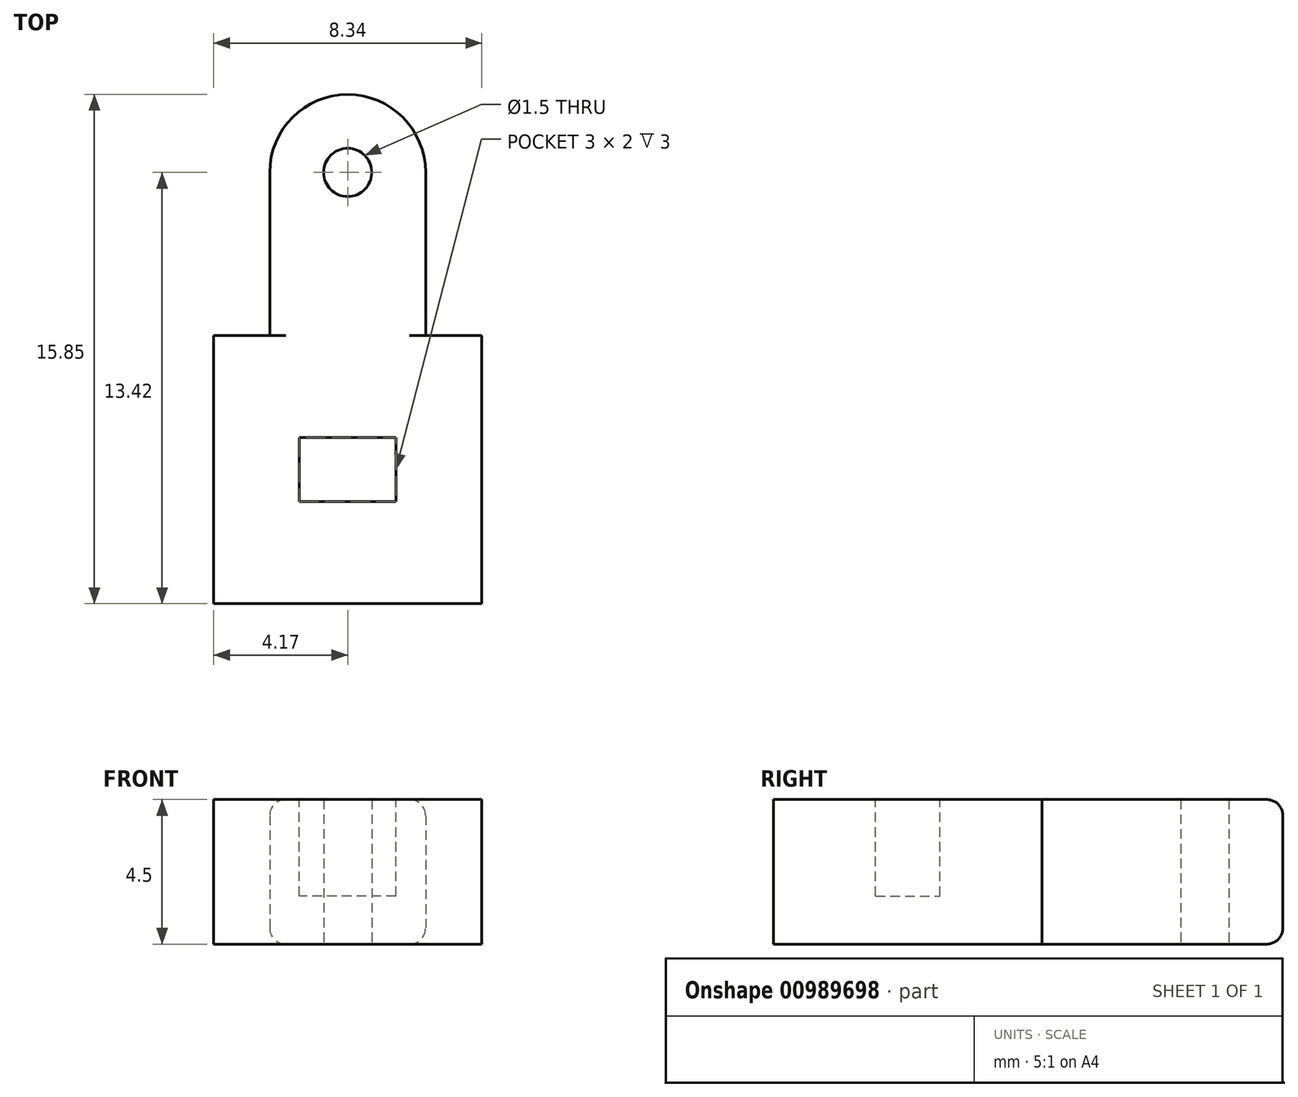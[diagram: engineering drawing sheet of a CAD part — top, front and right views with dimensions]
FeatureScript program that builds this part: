
annotation { "Feature Type Name" : "Feature", "Feature Type Description" : "" }
export const myFeature = defineFeature(function(context is Context, id is Id, definition is map)
    precondition{}
    {
        {
            var Q0;
            Q0=qCreatedBy(makeId("Top.planeOp"),FACE);
            var sketch = newSketch(context, id + "F0", { "sketchPlane" : qUnion([Q0])});
            skLineSegment(sketch, "E0.bottom", {"start": v(-4.18, 4.18) * mm, "end": v(4.18, 4.17) * mm});
            skLineSegment(sketch, "E0.top", {"start": v(-4.18, -4.17) * mm, "end": v(4.18, -4.18) * mm});
            skLineSegment(sketch, "E0.left", {"start": v(-4.17, 4.18) * mm, "end": v(-4.18, -4.18) * mm});
            skLineSegment(sketch, "E0.right", {"start": v(4.18, 4.18) * mm, "end": v(4.17, -4.18) * mm});
            skLineSegment(sketch, "E1", {"start": v(0, 4.17) * mm, "end": v(0, 11.67) * mm, "construction": true});
            skLineSegment(sketch, "E2", {"start": v(-2.42, 4.17) * mm, "end": v(-2.43, 9.25) * mm});
            skLineSegment(sketch, "E3", {"start": v(2.42, 4.17) * mm, "end": v(2.43, 9.25) * mm});
            skArc(sketch, "E4", {"start": v(2.42, 9.25) * mm, "mid": v(0, 11.67) * mm, "end": v(-2.43, 9.25) * mm});
            skCircle(sketch, "E5", {"center": v(0, 9.25) * mm, "radius": 0.75 * mm});
            skSolve(sketch);
        }
        {
            var Q0;
            Q0=makeQuery(id+"F0.imprint","IMPRINT",FACE,{"disambiguationData":[TD([[makeQuery(id+"F0.imprint","IMPRINT",EDGE,{"derivedFrom":sQuery(id+"F0.wireOp",EDGE,"E0.top")}),1.0]])]});
            var Q1;
            {var subQ1=sQuery(id+"F0.wireOp",EDGE,"E2");Q1=makeQuery(id+"F0.imprint","IMPRINT",FACE,{"disambiguationData":[TD([[makeQuery(id+"F0.imprint","IMPRINT",EDGE,{"derivedFrom":subQ1}),-1.0]])]});}
            extrude(context, id + "F1", {"entities" : qUnion([Q0, Q1]), "depth" : 4.5 * mm, "offsetDistance" : 25 * mm});
        }
        {
            var Q0;
            Q0=makeQuery(id+"F1.opExtrude","CAP_FACE",FACE,{"disambiguationData":[OSD([sQuery(id+"F0.wireOp",EDGE,"E0.bottom"),sQuery(id+"F0.wireOp",EDGE,"E0.top"),sQuery(id+"F0.wireOp",EDGE,"E0.left"),sQuery(id+"F0.wireOp",EDGE,"E0.right"),sQuery(id+"F0.wireOp",EDGE,"E2"),sQuery(id+"F0.wireOp",EDGE,"E3"),sQuery(id+"F0.wireOp",EDGE,"E4"),sQuery(id+"F0.wireOp",EDGE,"E5")])],"isStart":false});
            var sketch = newSketch(context, id + "F2", { "sketchPlane" : qUnion([Q0])});
            skLineSegment(sketch, "E6.bottom", {"start": v(1.5, -1) * mm, "end": v(-1.5, -1) * mm});
            skLineSegment(sketch, "E6.top", {"start": v(1.5, 1) * mm, "end": v(-1.5, 1) * mm});
            skLineSegment(sketch, "E6.left", {"start": v(1.5, -1) * mm, "end": v(1.5, 1) * mm});
            skLineSegment(sketch, "E6.right", {"start": v(-1.5, -1) * mm, "end": v(-1.5, 1) * mm});
            skSolve(sketch);
        }
        {
            var Q0;
            Q0=makeQuery(id+"F2.imprint","IMPRINT",FACE,{"disambiguationData":[TD([[makeQuery(id+"F2.imprint","IMPRINT",EDGE,{"derivedFrom":sQuery(id+"F2.wireOp",EDGE,"E6.bottom")}),-1.0]])]});
            extrude(context, id + "F3", {"entities" : qUnion([Q0]), "operationType" : NewBodyOperationType.REMOVE, "oppositeDirection" : true, "depth" : 3 * mm, "offsetDistance" : 25 * mm});
        }
        {
            var Q0;
            Q0=makeQuery(id+"F1.opExtrude","CAP_EDGE",EDGE,{"disambiguationData":[OSD([sQuery(id+"F0.wireOp",EDGE,"E4")])],"isStart":true});
            var Q1;
            Q1=makeQuery(id+"F1.opExtrude","CAP_EDGE",EDGE,{"disambiguationData":[OSD([sQuery(id+"F0.wireOp",EDGE,"E3")])],"isStart":true});
            var Q2;
            Q2=makeQuery(id+"F1.opExtrude","CAP_EDGE",EDGE,{"disambiguationData":[OSD([sQuery(id+"F0.wireOp",EDGE,"E2")])],"isStart":true});
            var Q3;
            Q3=makeQuery(id+"F1.opExtrude","CAP_EDGE",EDGE,{"disambiguationData":[OSD([sQuery(id+"F0.wireOp",EDGE,"E4")])],"isStart":false});
            var Q4;
            Q4=makeQuery(id+"F1.opExtrude","CAP_EDGE",EDGE,{"disambiguationData":[OSD([sQuery(id+"F0.wireOp",EDGE,"E3")])],"isStart":false});
            var Q5;
            Q5=makeQuery(id+"F1.opExtrude","CAP_EDGE",EDGE,{"disambiguationData":[OSD([sQuery(id+"F0.wireOp",EDGE,"E2")])],"isStart":false});
            fillet(context, id + "F4", {"entities" : qUnion([Q0, Q1, Q2, Q3, Q4, Q5]), "radius" : 0.5 * mm, "tangentPropagation" : true, "allowEdgeOverflow" : false});
        }
    });
